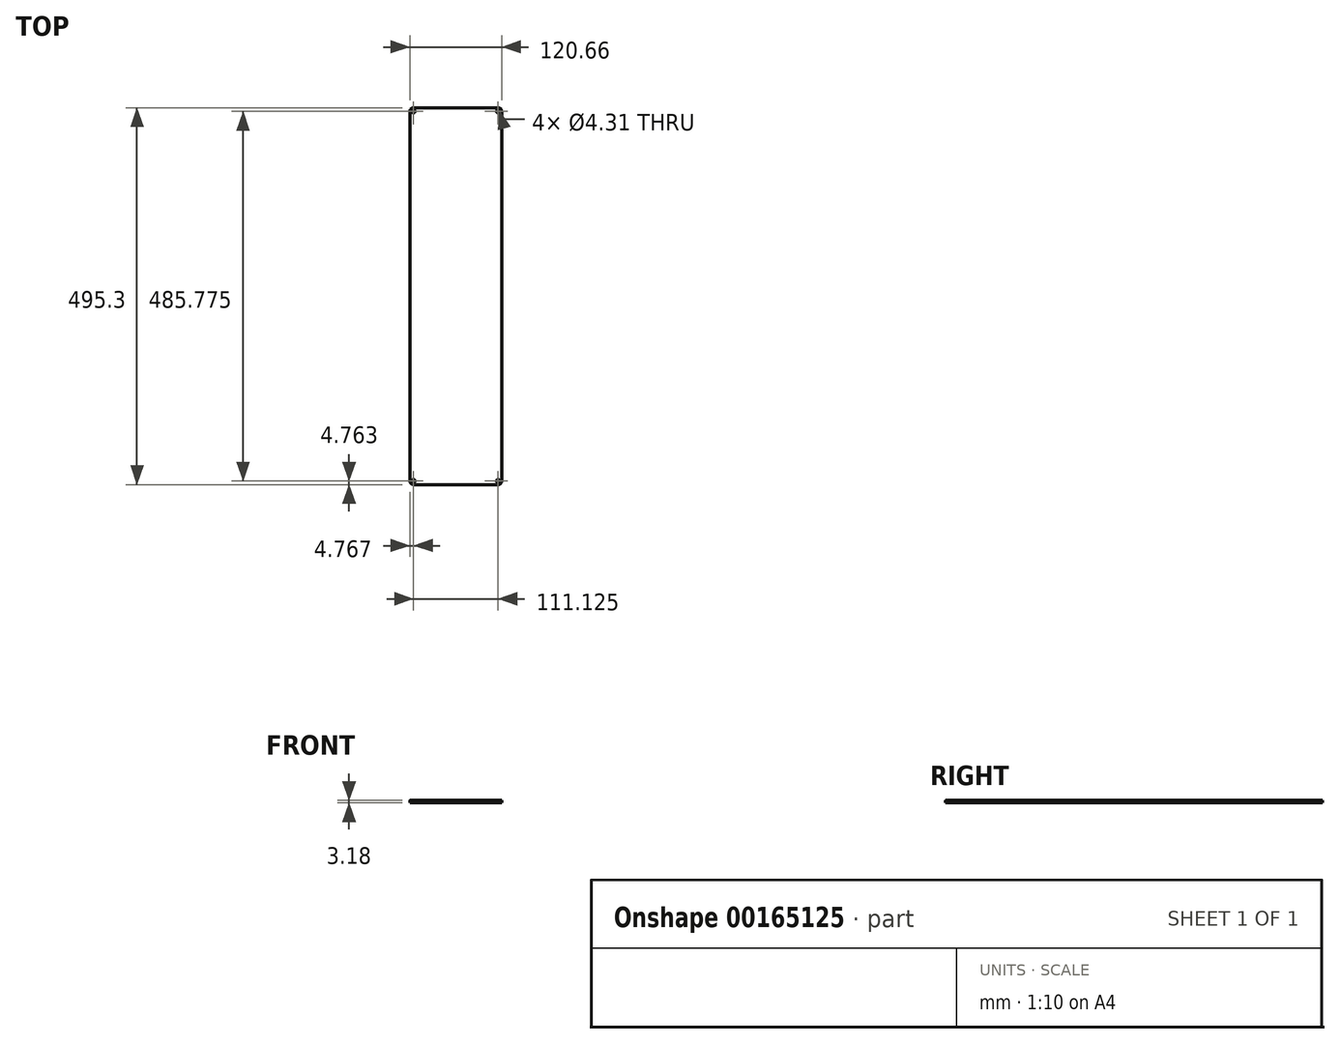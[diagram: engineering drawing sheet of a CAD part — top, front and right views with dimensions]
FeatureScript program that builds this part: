
annotation { "Feature Type Name" : "Feature", "Feature Type Description" : "" }
export const myFeature = defineFeature(function(context is Context, id is Id, definition is map)
    precondition{}
    {
        {
            var Q0;
            Q0=qCreatedBy(makeId("Top.planeOp"),FACE);
            var sketch = newSketch(context, id + "F0", { "sketchPlane" : qUnion([Q0])});
            skLineSegment(sketch, "E0.bottom", {"start": v(-60.33, 247.65) * mm, "end": v(60.32, 247.65) * mm});
            skLineSegment(sketch, "E0.top", {"start": v(-60.33, -247.65) * mm, "end": v(60.32, -247.65) * mm});
            skLineSegment(sketch, "E0.left", {"start": v(-60.33, 247.65) * mm, "end": v(-60.33, -247.65) * mm});
            skLineSegment(sketch, "E0.right", {"start": v(60.33, 247.65) * mm, "end": v(60.33, -247.65) * mm});
            skPoint(sketch, "E0.middle", {"position": v(0, 0) * mm});
            skLineSegment(sketch, "E1.bottom", {"start": v(-55.56, 242.89) * mm, "end": v(55.56, 242.89) * mm, "construction": true});
            skLineSegment(sketch, "E1.top", {"start": v(-55.56, -242.89) * mm, "end": v(55.56, -242.89) * mm, "construction": true});
            skLineSegment(sketch, "E1.left", {"start": v(-55.56, 242.89) * mm, "end": v(-55.56, -242.89) * mm, "construction": true});
            skLineSegment(sketch, "E1.right", {"start": v(55.56, 242.89) * mm, "end": v(55.56, -242.89) * mm, "construction": true});
            skLineSegment(sketch, "E2", {"start": v(0, 242.89) * mm, "end": v(0, 247.65) * mm, "construction": true});
            skLineSegment(sketch, "E3", {"start": v(-55.56, 0) * mm, "end": v(-60.33, 0) * mm, "construction": true});
            skCircle(sketch, "E4", {"center": v(-55.56, 242.89) * mm, "radius": 2.15 * mm});
            skCircle(sketch, "E5", {"center": v(-55.56, -242.89) * mm, "radius": 2.15 * mm});
            skCircle(sketch, "E6", {"center": v(55.56, -242.89) * mm, "radius": 2.15 * mm});
            skCircle(sketch, "E7", {"center": v(55.56, 242.89) * mm, "radius": 2.15 * mm});
            skSolve(sketch);
        }
        {
            var Q0;
            Q0=qSketchRegion(id+"F0",true);
            extrude(context, id + "F1", {"entities" : qUnion([Q0]), "depth" : 3.17 * mm});
        }
        {
            var Q0;
            Q0=makeQuery(id+"F1.opExtrude","SWEPT_EDGE",EDGE,{"disambiguationData":[OSD([sQuery(id+"F0.wireOp",EDGE,"E0.bottom"),sQuery(id+"F0.wireOp",EDGE,"E0.left")])]});
            var Q1;
            Q1=makeQuery(id+"F1.opExtrude","SWEPT_EDGE",EDGE,{"disambiguationData":[OSD([sQuery(id+"F0.wireOp",EDGE,"E0.bottom"),sQuery(id+"F0.wireOp",EDGE,"E0.right")])]});
            var Q2;
            Q2=makeQuery(id+"F1.opExtrude","SWEPT_EDGE",EDGE,{"disambiguationData":[OSD([sQuery(id+"F0.wireOp",EDGE,"E0.top"),sQuery(id+"F0.wireOp",EDGE,"E0.right")])]});
            var Q3;
            Q3=makeQuery(id+"F1.opExtrude","SWEPT_EDGE",EDGE,{"disambiguationData":[OSD([sQuery(id+"F0.wireOp",EDGE,"E0.top"),sQuery(id+"F0.wireOp",EDGE,"E0.left")])]});
            fillet(context, id + "F2", {"entities" : qUnion([Q0, Q1, Q2, Q3]), "radius" : 4.76 * mm, "tangentPropagation" : true, "allowEdgeOverflow" : false});
        }
    });
